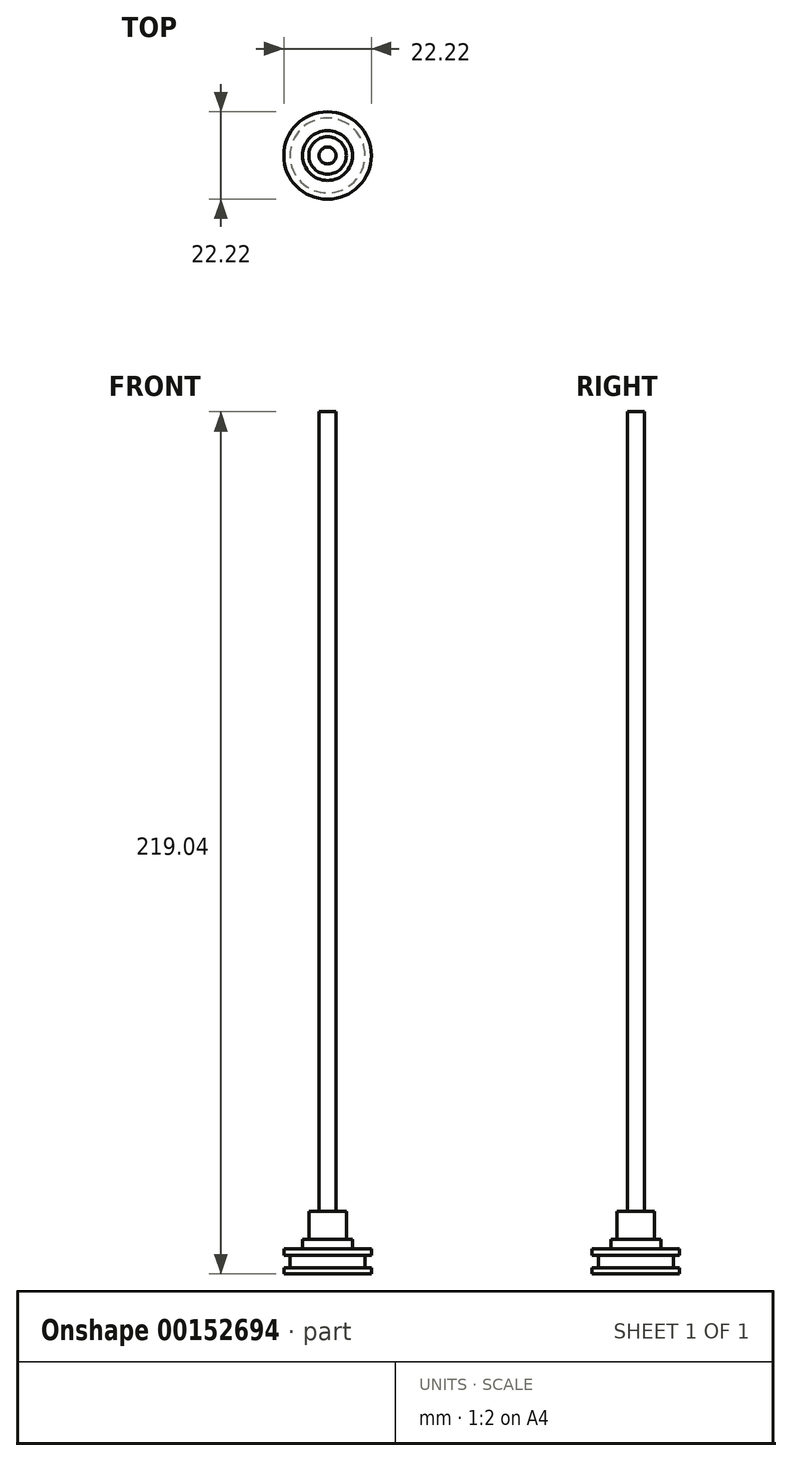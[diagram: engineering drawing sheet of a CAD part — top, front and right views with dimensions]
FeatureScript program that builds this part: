
annotation { "Feature Type Name" : "Feature", "Feature Type Description" : "" }
export const myFeature = defineFeature(function(context is Context, id is Id, definition is map)
    precondition{}
    {
        {
            var Q0;
            Q0=qCreatedBy(makeId("Top.planeOp"),FACE);
            var sketch = newSketch(context, id + "F0", { "sketchPlane" : qUnion([Q0])});
            skCircle(sketch, "E0", {"center": v(0, 0) * mm, "radius": 11.11 * mm});
            skSolve(sketch);
        }
        {
            var Q0;
            Q0 = qSketchRegion(id + "F0", true);
            extrude(context, id + "F1", {"entities" : qUnion([Q0]), "depth" : 1.59 * mm});
        }
        {
            var Q0;
            Q0=makeQuery(id+"F1.opExtrude","CAP_FACE",FACE,{"disambiguationData":[OSD([sQuery(id+"F0.wireOp",EDGE,"E0")])],"isStart":false});
            var sketch = newSketch(context, id + "F2", { "sketchPlane" : qUnion([Q0])});
            skCircle(sketch, "E1", {"center": v(0, 0) * mm, "radius": 9.53 * mm});
            skSolve(sketch);
        }
        {
            var Q0;
            Q0 = qSketchRegion(id + "F2", true);
            extrude(context, id + "F3", {"entities" : qUnion([Q0]), "operationType" : NewBodyOperationType.ADD, "depth" : 3.17 * mm});
        }
        {
            var Q0;
            Q0=makeQuery(id+"F3.opExtrude","CAP_FACE",FACE,{"disambiguationData":[OSD([sQuery(id+"F2.wireOp",EDGE,"E1")])],"isStart":false});
            var sketch = newSketch(context, id + "F4", { "sketchPlane" : qUnion([Q0])});
            skCircle(sketch, "E2", {"center": v(0, 0) * mm, "radius": 11.11 * mm});
            skSolve(sketch);
        }
        {
            var Q0;
            Q0 = qSketchRegion(id + "F4", true);
            extrude(context, id + "F5", {"entities" : qUnion([Q0]), "operationType" : NewBodyOperationType.ADD, "depth" : 1.59 * mm});
        }
        {
            var Q0;
            Q0=makeQuery(id+"F5.opExtrude","CAP_FACE",FACE,{"disambiguationData":[OSD([sQuery(id+"F4.wireOp",EDGE,"E2")])],"isStart":false});
            var sketch = newSketch(context, id + "F6", { "sketchPlane" : qUnion([Q0])});
            skCircle(sketch, "E3", {"center": v(0, 0) * mm, "radius": 6.35 * mm});
            skSolve(sketch);
        }
        {
            var Q0;
            Q0 = qSketchRegion(id + "F6", true);
            extrude(context, id + "F7", {"entities" : qUnion([Q0]), "operationType" : NewBodyOperationType.ADD, "depth" : 2.38 * mm});
        }
        {
            var Q0;
            Q0=makeQuery(id+"F7.opExtrude","CAP_FACE",FACE,{"disambiguationData":[OSD([sQuery(id+"F6.wireOp",EDGE,"E3")])],"isStart":false});
            var sketch = newSketch(context, id + "F8", { "sketchPlane" : qUnion([Q0])});
            skCircle(sketch, "E4", {"center": v(0, 0) * mm, "radius": 4.76 * mm});
            skSolve(sketch);
        }
        {
            var Q0;
            Q0 = qSketchRegion(id + "F8", true);
            extrude(context, id + "F9", {"entities" : qUnion([Q0]), "operationType" : NewBodyOperationType.ADD, "depth" : 7.11 * mm});
        }
        {
            var Q0;
            Q0=makeQuery(id+"F9.opExtrude","CAP_FACE",FACE,{"disambiguationData":[OSD([sQuery(id+"F8.wireOp",EDGE,"E4")])],"isStart":false});
            var sketch = newSketch(context, id + "F10", { "sketchPlane" : qUnion([Q0])});
            skCircle(sketch, "E5", {"center": v(0, 0) * mm, "radius": 2.15 * mm});
            skSolve(sketch);
        }
        {
            var Q0;
            Q0 = qSketchRegion(id + "F10", true);
            extrude(context, id + "F11", {"entities" : qUnion([Q0]), "operationType" : NewBodyOperationType.ADD, "depth" : 203.2 * mm});
        }
    });
